# Revit family: 49060XXX
name_source: partatom
category: Plumbing Fixtures
units: mm (PartAtom-declared; Revit-internal decimal feet)

## family parameters
Always vertical = No
Cut with Voids When Loaded = No
OmniClass Number = 23.31.11.00
OmniClass Title = Faucets
Part Type = Normal
Room Calculation Point = No
Round Connector Dimension = Use Diameter
Shared = No
Work Plane-Based = Yes

## types (12) — shared parameters
Connector Description = Water Inlet 9.5mm
Default Elevation = 1219 mm
Description = AXOR Citterio C 3-hole basin mixer 125 with pop-up waste set
Diameter = 10 mm  [stored 0.0328084 ft]
Manufacturer = AXOR
Model = 49060XXX
Product Guid = a91c48ef-0867-4c13-8a3e-02a21c0314cb
Product Page URL = https://www.axor-design.com
Product data url = https://bimobject.com
URL = https://www.axor-design.com
Version = 1

## per-type parameters (varying)
| type | Material |
| 800 Stainless Steel Optic | AXOR - Metal - 800 Stainless Steel Optic |
| 330 Polished Black Chrome | AXOR - Metal - 330 Polished Black Chrome |
| 820 Brushed Nickel | AXOR - Metal - 820 Brushed Nickel |
| 340 Brushed Black Chrome | AXOR - Metal - 340 Brushed Black Chrome |
| 250 Brushed Gold Optic | AXOR - Metal - 250 Brushed Gold Optic |
| 990 Polished Gold Optic | AXOR - Metal - 990 Polished Gold Optic |
| 140 Brushed Bronze | AXOR - Metal - 140 Brushed Bronze |
| 950 Brushed Brass | AXOR - Metal - 950 Brushed Brass |
| 310 Brushed Red Gold | AXOR - Metal - 310 Brushed Red Gold |
| 300 Polished Red Gold | AXOR - Metal - 300 Polished Red Gold |
| 000 Chrome | AXOR - Metal - 000 Chrome |
| 670 Matte Black | AXOR - Metal - 670 Matte Black |

note: [stored X ft] marks values corroborated as IEEE doubles in the binary element streams (Revit-internal decimal feet)

## geometry (parser evidence)
native form markers: Sweep x2
no freeform markers — native parametric forms only
